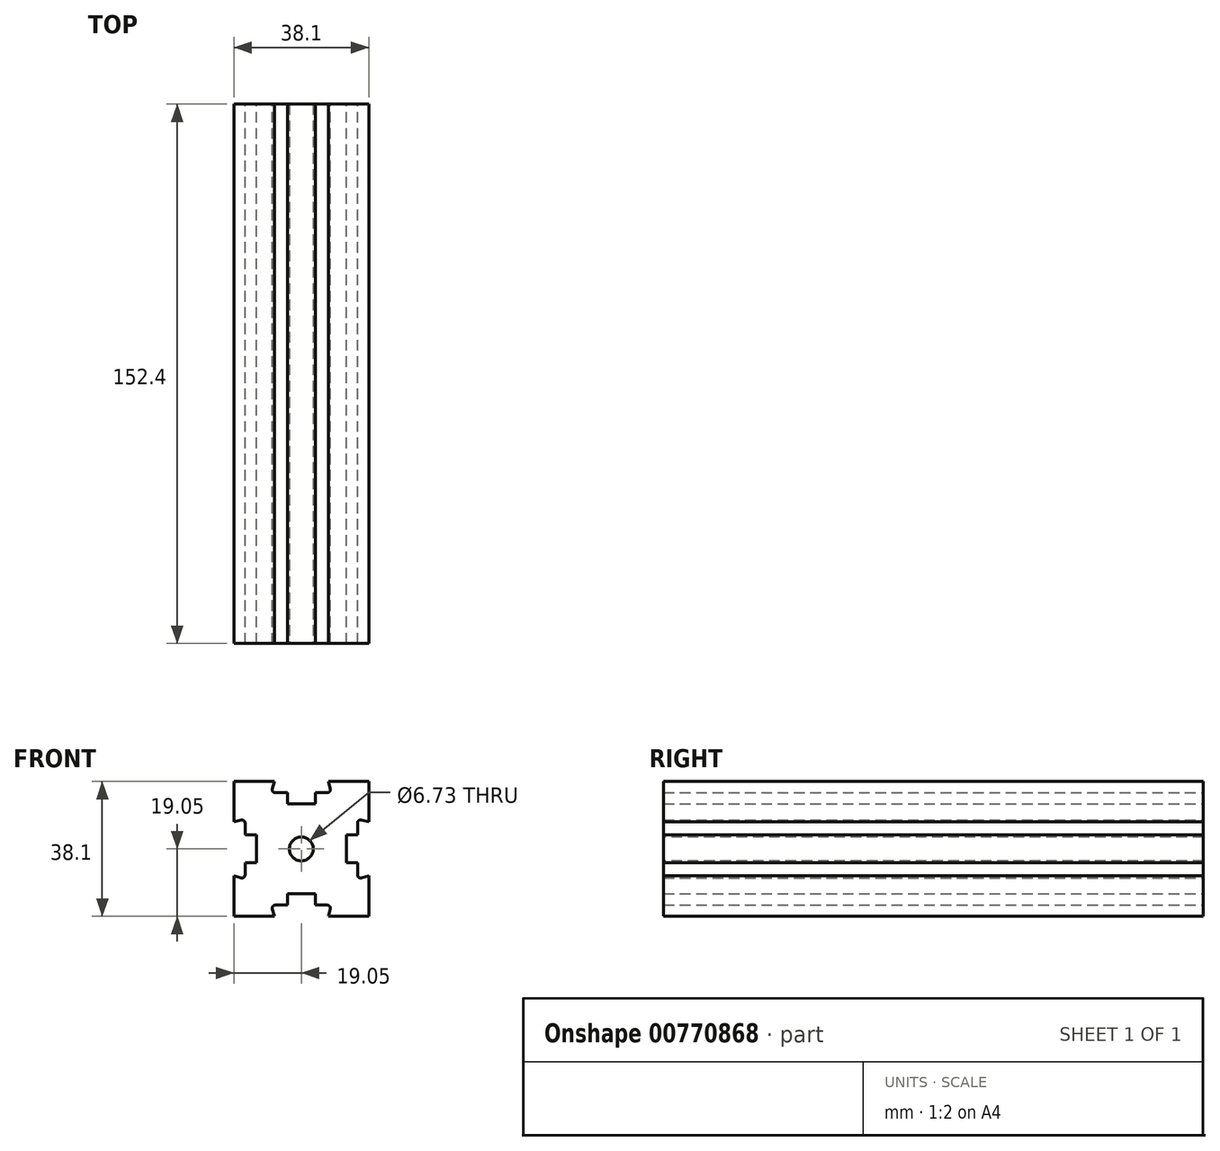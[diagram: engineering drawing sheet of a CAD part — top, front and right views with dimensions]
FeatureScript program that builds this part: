
annotation { "Feature Type Name" : "Feature", "Feature Type Description" : "" }
export const myFeature = defineFeature(function(context is Context, id is Id, definition is map)
    precondition{}
    {
        {
            var Q0;
            Q0=qCreatedBy(makeId("Front.planeOp"),FACE);
            var sketch = newSketch(context, id + "F0", { "sketchPlane" : qUnion([Q0])});
            skLineSegment(sketch, "E0", {"start": v(21.9, 21.9) * mm, "end": v(0, 0) * mm, "construction": true});
            skLineSegment(sketch, "E1", {"start": v(3.94, 12.7) * mm, "end": v(3.94, 15.88) * mm});
            skLineSegment(sketch, "E2", {"start": v(3.94, 15.88) * mm, "end": v(7.32, 15.88) * mm});
            skLineSegment(sketch, "E3", {"start": v(8.17, 16.99) * mm, "end": v(7.62, 19.05) * mm});
            skLineSegment(sketch, "E4", {"start": v(7.62, 19.05) * mm, "end": v(19.05, 19.05) * mm});
            skLineSegment(sketch, "E5.MirrorCS", {"start": v(15.88, 3.94) * mm, "end": v(15.88, 7.32) * mm});
            skLineSegment(sketch, "E6.MirrorCS", {"start": v(12.7, 3.94) * mm, "end": v(15.88, 3.94) * mm});
            skLineSegment(sketch, "E7.MirrorCS", {"start": v(19.05, 7.62) * mm, "end": v(19.05, 19.05) * mm});
            skLineSegment(sketch, "E8.MirrorCS", {"start": v(16.99, 8.17) * mm, "end": v(19.05, 7.62) * mm});
            skLineSegment(sketch, "E9.MirrorCS", {"start": v(-7.62, 19.05) * mm, "end": v(-19.05, 19.05) * mm});
            skLineSegment(sketch, "E10.MirrorCS", {"start": v(-19.05, 7.62) * mm, "end": v(-19.05, 19.05) * mm});
            skLineSegment(sketch, "E11.MirrorCS", {"start": v(-16.99, 8.17) * mm, "end": v(-19.05, 7.62) * mm});
            skLineSegment(sketch, "E12.MirrorCS", {"start": v(-8.17, 16.99) * mm, "end": v(-7.62, 19.05) * mm});
            skLineSegment(sketch, "E13.MirrorCS", {"start": v(-3.94, 12.7) * mm, "end": v(-3.94, 15.88) * mm});
            skLineSegment(sketch, "E14.MirrorCS", {"start": v(-12.7, 3.94) * mm, "end": v(-15.88, 3.94) * mm});
            skLineSegment(sketch, "E15.MirrorCS", {"start": v(-15.88, 3.94) * mm, "end": v(-15.88, 7.32) * mm});
            skLineSegment(sketch, "E16.MirrorCS", {"start": v(-3.94, 15.88) * mm, "end": v(-7.32, 15.88) * mm});
            skLineSegment(sketch, "E17.MirrorCS", {"start": v(-19.05, -7.62) * mm, "end": v(-19.05, -19.05) * mm});
            skLineSegment(sketch, "E18.MirrorCS", {"start": v(3.94, -15.88) * mm, "end": v(7.32, -15.88) * mm});
            skLineSegment(sketch, "E19.MirrorCS", {"start": v(12.7, -3.94) * mm, "end": v(15.88, -3.94) * mm});
            skLineSegment(sketch, "E20.MirrorCS", {"start": v(8.17, -16.99) * mm, "end": v(7.62, -19.05) * mm});
            skLineSegment(sketch, "E21.MirrorCS", {"start": v(16.99, -8.17) * mm, "end": v(19.05, -7.62) * mm});
            skLineSegment(sketch, "E22.MirrorCS", {"start": v(19.05, -7.62) * mm, "end": v(19.05, -19.05) * mm});
            skLineSegment(sketch, "E23.MirrorCS", {"start": v(-8.17, -16.99) * mm, "end": v(-7.62, -19.05) * mm});
            skLineSegment(sketch, "E24.MirrorCS", {"start": v(7.62, -19.05) * mm, "end": v(19.05, -19.05) * mm});
            skLineSegment(sketch, "E25.MirrorCS", {"start": v(-3.94, -12.7) * mm, "end": v(-3.94, -15.88) * mm});
            skLineSegment(sketch, "E26.MirrorCS", {"start": v(-3.94, -15.88) * mm, "end": v(-7.32, -15.88) * mm});
            skLineSegment(sketch, "E27.MirrorCS", {"start": v(-12.7, -3.94) * mm, "end": v(-15.88, -3.94) * mm});
            skLineSegment(sketch, "E28.MirrorCS", {"start": v(15.88, -3.94) * mm, "end": v(15.88, -7.32) * mm});
            skLineSegment(sketch, "E29.MirrorCS", {"start": v(-15.88, -3.94) * mm, "end": v(-15.88, -7.32) * mm});
            skLineSegment(sketch, "E30.MirrorCS", {"start": v(-16.99, -8.17) * mm, "end": v(-19.05, -7.62) * mm});
            skLineSegment(sketch, "E31.MirrorCS", {"start": v(3.94, -12.7) * mm, "end": v(3.94, -15.88) * mm});
            skLineSegment(sketch, "E32.MirrorCS", {"start": v(-7.62, -19.05) * mm, "end": v(-19.05, -19.05) * mm});
            skLineSegment(sketch, "E33", {"start": v(3.94, 12.7) * mm, "end": v(-3.94, 12.7) * mm});
            skLineSegment(sketch, "E34", {"start": v(-12.7, 3.94) * mm, "end": v(-12.7, -3.94) * mm});
            skLineSegment(sketch, "E35", {"start": v(12.7, 3.94) * mm, "end": v(12.7, -3.94) * mm});
            skLineSegment(sketch, "E36", {"start": v(3.94, -12.7) * mm, "end": v(-3.94, -12.7) * mm});
            skPoint(sketch, "E37.visualSharp", {"position": v(8.47, 15.88) * mm});
            skArc(sketch, "E37.filletArc", {"start": v(7.32, 15.88) * mm, "mid": v(8.02, 16.22) * mm, "end": v(8.17, 16.99) * mm});
            skPoint(sketch, "E38.visualSharp", {"position": v(-8.47, 15.88) * mm});
            skArc(sketch, "E38.filletArc", {"start": v(-8.17, 16.99) * mm, "mid": v(-8.02, 16.22) * mm, "end": v(-7.32, 15.88) * mm});
            skPoint(sketch, "E39.visualSharp", {"position": v(15.88, 8.47) * mm});
            skArc(sketch, "E39.filletArc", {"start": v(16.99, 8.17) * mm, "mid": v(16.22, 8.02) * mm, "end": v(15.88, 7.32) * mm});
            skPoint(sketch, "E40.visualSharp", {"position": v(15.88, -8.47) * mm});
            skArc(sketch, "E40.filletArc", {"start": v(15.88, -7.32) * mm, "mid": v(16.22, -8.02) * mm, "end": v(16.99, -8.17) * mm});
            skPoint(sketch, "E41.visualSharp", {"position": v(-8.47, -15.88) * mm});
            skArc(sketch, "E41.filletArc", {"start": v(-7.32, -15.88) * mm, "mid": v(-8.02, -16.22) * mm, "end": v(-8.17, -16.99) * mm});
            skPoint(sketch, "E42.visualSharp", {"position": v(8.47, -15.88) * mm});
            skArc(sketch, "E42.filletArc", {"start": v(8.17, -16.99) * mm, "mid": v(8.02, -16.22) * mm, "end": v(7.32, -15.88) * mm});
            skPoint(sketch, "E43.visualSharp", {"position": v(-15.88, -8.47) * mm});
            skArc(sketch, "E43.filletArc", {"start": v(-16.99, -8.17) * mm, "mid": v(-16.22, -8.02) * mm, "end": v(-15.88, -7.32) * mm});
            skPoint(sketch, "E44.visualSharp", {"position": v(-15.88, 8.47) * mm});
            skArc(sketch, "E44.filletArc", {"start": v(-15.88, 7.32) * mm, "mid": v(-16.22, 8.02) * mm, "end": v(-16.99, 8.17) * mm});
            skSolve(sketch);
        }
        {
            var Q0;
            Q0=makeQuery(id+"F0.imprint","IMPRINT",FACE,{"disambiguationData":[TD([[makeQuery(id+"F0.imprint","IMPRINT",EDGE,{"derivedFrom":sQuery(id+"F0.wireOp",EDGE,"E1")}),-1.0]])]});
            extrude(context, id + "F1", {"entities" : qUnion([Q0]), "depth" : 152.4 * mm, "offsetDistance" : 25.4 * mm});
        }
        {
            var Q0;
            Q0=makeQuery(id+"F1.opExtrude","CAP_FACE",FACE,{"disambiguationData":[OSD([sQuery(id+"F0.wireOp",EDGE,"E1"),sQuery(id+"F0.wireOp",EDGE,"E2"),sQuery(id+"F0.wireOp",EDGE,"E3"),sQuery(id+"F0.wireOp",EDGE,"E4"),sQuery(id+"F0.wireOp",EDGE,"E5.MirrorCS"),sQuery(id+"F0.wireOp",EDGE,"E6.MirrorCS"),sQuery(id+"F0.wireOp",EDGE,"E7.MirrorCS"),sQuery(id+"F0.wireOp",EDGE,"E8.MirrorCS"),sQuery(id+"F0.wireOp",EDGE,"E9.MirrorCS"),sQuery(id+"F0.wireOp",EDGE,"E10.MirrorCS"),sQuery(id+"F0.wireOp",EDGE,"E11.MirrorCS"),sQuery(id+"F0.wireOp",EDGE,"E12.MirrorCS"),sQuery(id+"F0.wireOp",EDGE,"E13.MirrorCS"),sQuery(id+"F0.wireOp",EDGE,"E14.MirrorCS"),sQuery(id+"F0.wireOp",EDGE,"E15.MirrorCS"),sQuery(id+"F0.wireOp",EDGE,"E16.MirrorCS"),sQuery(id+"F0.wireOp",EDGE,"E17.MirrorCS"),sQuery(id+"F0.wireOp",EDGE,"E18.MirrorCS"),sQuery(id+"F0.wireOp",EDGE,"E19.MirrorCS"),sQuery(id+"F0.wireOp",EDGE,"E20.MirrorCS"),sQuery(id+"F0.wireOp",EDGE,"E21.MirrorCS"),sQuery(id+"F0.wireOp",EDGE,"E22.MirrorCS"),sQuery(id+"F0.wireOp",EDGE,"E23.MirrorCS"),sQuery(id+"F0.wireOp",EDGE,"E24.MirrorCS"),sQuery(id+"F0.wireOp",EDGE,"E25.MirrorCS"),sQuery(id+"F0.wireOp",EDGE,"E26.MirrorCS"),sQuery(id+"F0.wireOp",EDGE,"E27.MirrorCS"),sQuery(id+"F0.wireOp",EDGE,"E28.MirrorCS"),sQuery(id+"F0.wireOp",EDGE,"E29.MirrorCS"),sQuery(id+"F0.wireOp",EDGE,"E30.MirrorCS"),sQuery(id+"F0.wireOp",EDGE,"E31.MirrorCS"),sQuery(id+"F0.wireOp",EDGE,"E32.MirrorCS"),sQuery(id+"F0.wireOp",EDGE,"E33"),sQuery(id+"F0.wireOp",EDGE,"E34"),sQuery(id+"F0.wireOp",EDGE,"E35"),sQuery(id+"F0.wireOp",EDGE,"E36")])],"isStart":false});
            var sketch = newSketch(context, id + "F2", { "sketchPlane" : qUnion([Q0])});
            skCircle(sketch, "E45", {"center": v(0, 0) * mm, "radius": 3.37 * mm});
            skSolve(sketch);
        }
        {
            var Q0;
            Q0=makeQuery(id+"F2.imprint","IMPRINT",FACE,{"disambiguationData":[TD([[makeQuery(id+"F2.imprint","IMPRINT",EDGE,{"derivedFrom":sQuery(id+"F2.wireOp",EDGE,"E45")}),1.0]])]});
            extrude(context, id + "F3", {"entities" : qUnion([Q0]), "operationType" : NewBodyOperationType.REMOVE, "endBound" : BoundingType.THROUGH_ALL, "oppositeDirection" : true, "depth" : 25.4 * mm, "offsetDistance" : 25.4 * mm});
        }
    });
